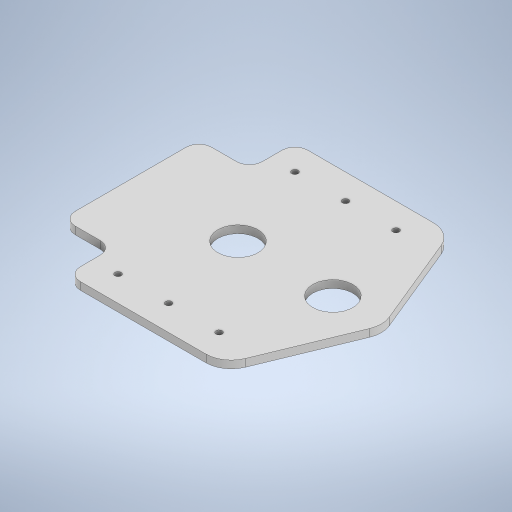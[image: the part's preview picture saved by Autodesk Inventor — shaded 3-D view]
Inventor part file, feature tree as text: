
AUTODESK INVENTOR PART (.ipt)
format: ipt  version: 2023 (Build 270158000, 158)  size: 274,432 bytes
history: native  units: in
note: dims shown in document units (in); Inventor stores cm internally (conversion verified against a paired STEP export)
features: extrude x1, sketch x1
ambient origin geometry x8: Origin, YZ Plane, XZ Plane, XY Plane, X Axis, Y Axis, Z Axis, Center Point
bodies: Solid1 (feature_tree)
feature tree (2):
  extrude  "Extrusion1"  Depth=3.5433in
  sketch  "Sketch1"  dims[d0=3.5433in d1=3.5433in d2=0.7874in d3=2.126in d4=0.7087in d5=0.0984in d6=0.7874in d8=2.7559in d9=1.9685in d11=0.7874in d14=0.625in d15=1.5748in d17=0.2756in d18=3.5039in d19=0.2756in d20=0.0in d21=2.8346in d22=0.3543in d23=0.3937in d24=0.3937in d25=0.1969in d26=1.4781in d27=0.625in d28=0.1181in d29=0.0in]
